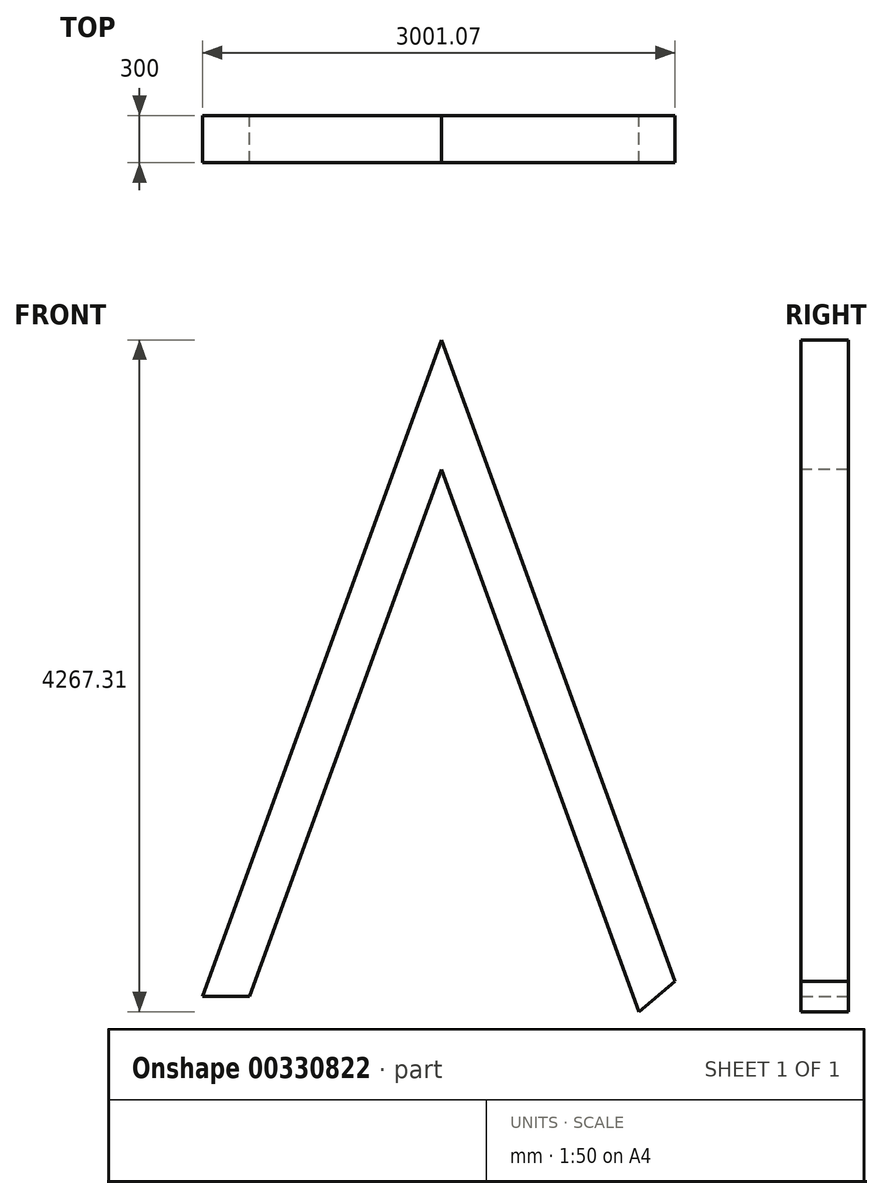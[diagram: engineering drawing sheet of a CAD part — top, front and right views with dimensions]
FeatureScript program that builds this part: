
annotation { "Feature Type Name" : "Feature", "Feature Type Description" : "" }
export const myFeature = defineFeature(function(context is Context, id is Id, definition is map)
    precondition{}
    {
        {
            var Q0;
            Q0=qCreatedBy(makeId("Top.planeOp"),FACE);
            var sketch = newSketch(context, id + "F0", { "sketchPlane" : qUnion([Q0])});
            skLineSegment(sketch, "E0.bottom", {"start": v(150, -150) * mm, "end": v(-150, -150) * mm});
            skLineSegment(sketch, "E0.top", {"start": v(150, 150) * mm, "end": v(-150, 150) * mm});
            skLineSegment(sketch, "E0.left", {"start": v(150, -150) * mm, "end": v(150, 150) * mm});
            skLineSegment(sketch, "E0.right", {"start": v(-150, -150) * mm, "end": v(-150, 150) * mm});
            skPoint(sketch, "E0.middle", {"position": v(0, 0) * mm});
            skSolve(sketch);
        }
        {
            var Q0;
            Q0=qCreatedBy(makeId("Front.planeOp"),FACE);
            var sketch = newSketch(context, id + "F1", { "sketchPlane" : qUnion([Q0])});
            skLineSegment(sketch, "E1", {"start": v(0, 0) * mm, "end": v(1368.08, 3758.77) * mm});
            skLineSegment(sketch, "E2", {"start": v(1368.08, 3758.77) * mm, "end": v(1368.08, 0) * mm, "construction": true});
            skLineSegment(sketch, "E3.MirrorCS", {"start": v(2736.16, 0) * mm, "end": v(1368.08, 3758.77) * mm});
            skSolve(sketch);
        }
        {
            var Q0;
            Q0 = qSketchRegion(id + "F0", true);
            var Q1;
            Q1=sQuery(id+"F1.wireOp",EDGE,"E1");
            var Q2;
            Q2=sQuery(id+"F1.wireOp",EDGE,"E3.MirrorCS");
            sweep(context, id + "F2", {"profiles" : qUnion([Q0]), "path" : qUnion([Q1, Q2])});
        }
    });
